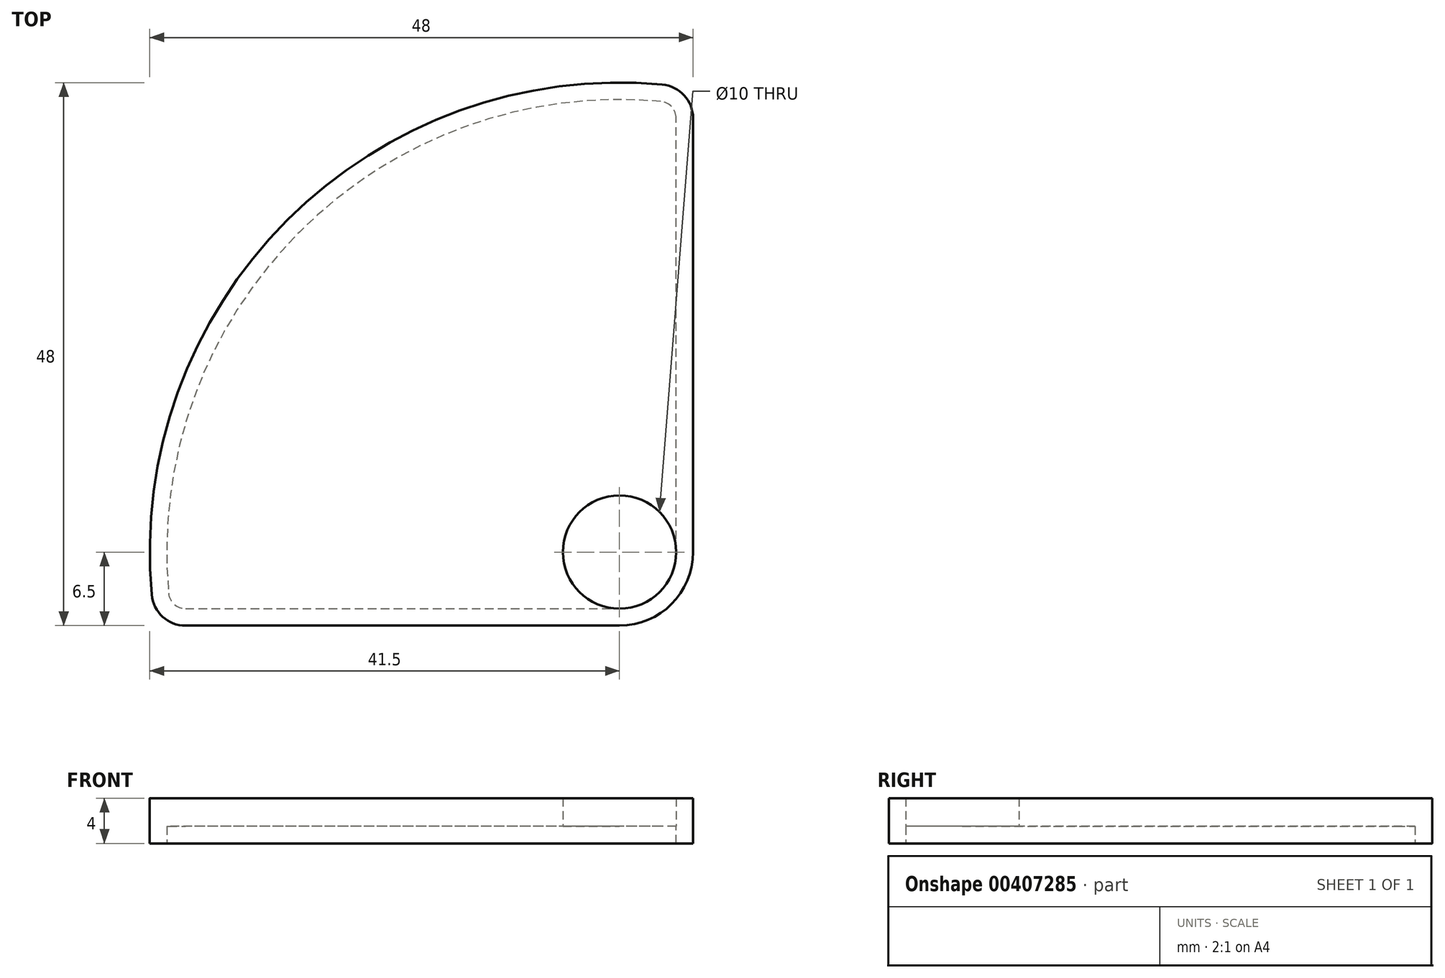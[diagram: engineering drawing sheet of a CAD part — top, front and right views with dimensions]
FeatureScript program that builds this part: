
annotation { "Feature Type Name" : "Feature", "Feature Type Description" : "" }
export const myFeature = defineFeature(function(context is Context, id is Id, definition is map)
    precondition{}
    {
        {
            var Q0;
            Q0=qCreatedBy(makeId("Top.planeOp"),FACE);
            var sketch = newSketch(context, id + "F0", { "sketchPlane" : qUnion([Q0])});
            skLineSegment(sketch, "E0", {"start": v(0, 6.5) * mm, "end": v(0, 47.49) * mm});
            skLineSegment(sketch, "E1", {"start": v(-13, 0) * mm, "end": v(-6.5, 0) * mm});
            skPoint(sketch, "E2.visualSharp", {"position": v(0, 0) * mm});
            skArc(sketch, "E2.filletArc", {"start": v(-6.5, 0) * mm, "mid": v(-1.9, 1.9) * mm, "end": v(0, 6.5) * mm});
            skLineSegment(sketch, "E3", {"start": v(-6.5, 0) * mm, "end": v(-6.5, 6.5) * mm, "construction": true});
            skLineSegment(sketch, "E4", {"start": v(0, 6.5) * mm, "end": v(-6.5, 6.5) * mm, "construction": true});
            skArc(sketch, "E5", {"start": v(-47.49, 0) * mm, "mid": v(-35.84, 35.84) * mm, "end": v(0, 47.49) * mm, "construction": true});
            skArc(sketch, "E6", {"start": v(-47.49, 0) * mm, "mid": v(-35.84, 35.84) * mm, "end": v(0, 47.49) * mm});
            skLineSegment(sketch, "E7", {"start": v(-13, 0) * mm, "end": v(-47.49, 0) * mm});
            skSolve(sketch);
        }
        {
            var Q0;
            Q0=makeQuery(id+"F0.imprint","IMPRINT",FACE,{"disambiguationData":[TD([[makeQuery(id+"F0.imprint","IMPRINT",EDGE,{"derivedFrom":sQuery(id+"F0.wireOp",EDGE,"E0")}),1.0]])]});
            extrude(context, id + "F1", {"entities" : qUnion([Q0]), "depth" : 4 * mm});
        }
        {
            var Q0;
            Q0=makeQuery(id+"F1.opExtrude","CAP_FACE",FACE,{"disambiguationData":[OSD([sQuery(id+"F0.wireOp",EDGE,"NLBvzQAC-VEYf-z00a-SUDr-PS6Iiug7ZcWT"),sQuery(id+"F0.wireOp",EDGE,"vp4aBCBo-WHFW-VkR4-K5s5-xs8t65EtAtv6"),sQuery(id+"F0.wireOp",EDGE,"E0")])],"isStart":false});
            var Q1;
            Q1=makeQuery(id+"F1.opExtrude","CAP_FACE",FACE,{"disambiguationData":[OSD([sQuery(id+"F0.wireOp",EDGE,"NLBvzQAC-VEYf-z00a-SUDr-PS6Iiug7ZcWT"),sQuery(id+"F0.wireOp",EDGE,"E0"),sQuery(id+"F0.wireOp",EDGE,"sY9fAtrw-aqXI-RMX0-P5VE-8Oq5YwFjua6t"),sQuery(id+"F0.wireOp",EDGE,"c47a2967-c131-48a5-880a-628ae06fc696.trimOffspring")])],"isStart":true});
            shell(context, id + "F2", {"entities" : qUnion([Q0, Q1]), "thickness" : 1.5 * mm});
        }
        {
            var Q0;
            Q0=qCreatedBy(makeId("Top.planeOp"),FACE);
            cPlane(context, id + "F3", {"entities" : qUnion([Q0]), "cplaneType" : CPlaneType.OFFSET, "offset" : 1.5 * mm, "width" : 150 * mm, "height" : 150 * mm});
        }
        {
            var Q0;
            Q0=qCreatedBy(id+"F3.planeOp",FACE);
            var sketch = newSketch(context, id + "F4", { "sketchPlane" : qUnion([Q0])});
            skLineSegment(sketch, "E8.0", {"start": v(-6.5, 1.5) * mm, "end": v(-46.19, 1.5) * mm});
            skPoint(sketch, "E9.0", {"position": v(-2.96, 2.96) * mm});
            skArc(sketch, "E10.0", {"start": v(-6.5, 1.5) * mm, "mid": v(-2.96, 2.96) * mm, "end": v(-1.5, 6.5) * mm});
            skLineSegment(sketch, "E11.0", {"start": v(-1.5, 6.5) * mm, "end": v(-1.5, 46.19) * mm});
            skArc(sketch, "E12.0", {"start": v(-46.19, 1.5) * mm, "mid": v(-34.78, 34.78) * mm, "end": v(-1.5, 46.19) * mm});
            skSolve(sketch);
        }
        {
            var Q0;
            Q0=makeQuery(id+"F4.imprint","IMPRINT",FACE,{"disambiguationData":[TD([[makeQuery(id+"F4.imprint","IMPRINT",EDGE,{"derivedFrom":sQuery(id+"F4.wireOp",EDGE,"E8.0")}),-1.0]])]});
            extrude(context, id + "F5", {"entities" : qUnion([Q0]), "operationType" : NewBodyOperationType.ADD, "depth" : 2.5 * mm});
        }
        {
            var Q0;
            Q0=makeQuery(id+"F2.opShell","OFFSET_EDGE",EDGE,{"disambiguationData":[OSD([sQuery(id+"F0.wireOp",EDGE,"E0"),sQuery(id+"F0.wireOp",EDGE,"E6")])]});
            var Q1;
            Q1=makeQuery(id+"F2.opShell","OFFSET_EDGE",EDGE,{"disambiguationData":[OSD([sQuery(id+"F0.wireOp",EDGE,"E6"),sQuery(id+"F0.wireOp",EDGE,"E7")])]});
            fillet(context, id + "F6", {"entities" : qUnion([Q0, Q1]), "radius" : 1.5 * mm, "tangentPropagation" : true, "allowEdgeOverflow" : false});
        }
        {
            var Q0;
            Q0=makeQuery(id+"F1.opExtrude","SWEPT_EDGE",EDGE,{"disambiguationData":[OSD([sQuery(id+"F0.wireOp",EDGE,"E6"),sQuery(id+"F0.wireOp",EDGE,"E7")])]});
            var Q1;
            Q1=makeQuery(id+"F1.opExtrude","SWEPT_EDGE",EDGE,{"disambiguationData":[OSD([sQuery(id+"F0.wireOp",EDGE,"E0"),sQuery(id+"F0.wireOp",EDGE,"E6")])]});
            fillet(context, id + "F7", {"entities" : qUnion([Q0, Q1]), "radius" : 3 * mm, "tangentPropagation" : true, "allowEdgeOverflow" : false});
        }
        {
            var Q0;
            Q0=makeQuery(id+"F1.opExtrude","CAP_FACE",FACE,{"disambiguationData":[OSD([sQuery(id+"F0.wireOp",EDGE,"E0"),sQuery(id+"F0.wireOp",EDGE,"E1"),sQuery(id+"F0.wireOp",EDGE,"E2.filletArc"),sQuery(id+"F0.wireOp",EDGE,"E6"),sQuery(id+"F0.wireOp",EDGE,"E7")])],"isStart":true});
            var sketch = newSketch(context, id + "F8", { "sketchPlane" : qUnion([Q0])});
            skArc(sketch, "E13.0", {"start": v(-6.5, -1.5) * mm, "mid": v(-2.96, -2.96) * mm, "end": v(-1.5, -6.5) * mm});
            skArc(sketch, "E14", {"start": v(-6.5, -1.5) * mm, "mid": v(-10.04, -10.04) * mm, "end": v(-1.5, -6.5) * mm});
            skSolve(sketch);
        }
        {
            var Q0;
            Q0=makeQuery(id+"F8.imprint","IMPRINT",FACE,{"disambiguationData":[TD([[makeQuery(id+"F8.imprint","IMPRINT",EDGE,{"derivedFrom":sQuery(id+"F8.wireOp",EDGE,"E13.0")}),-1.0]])]});
            extrude(context, id + "F9", {"entities" : qUnion([Q0]), "operationType" : NewBodyOperationType.REMOVE, "endBound" : BoundingType.THROUGH_ALL, "oppositeDirection" : true, "depth" : 25 * mm});
        }
    });
